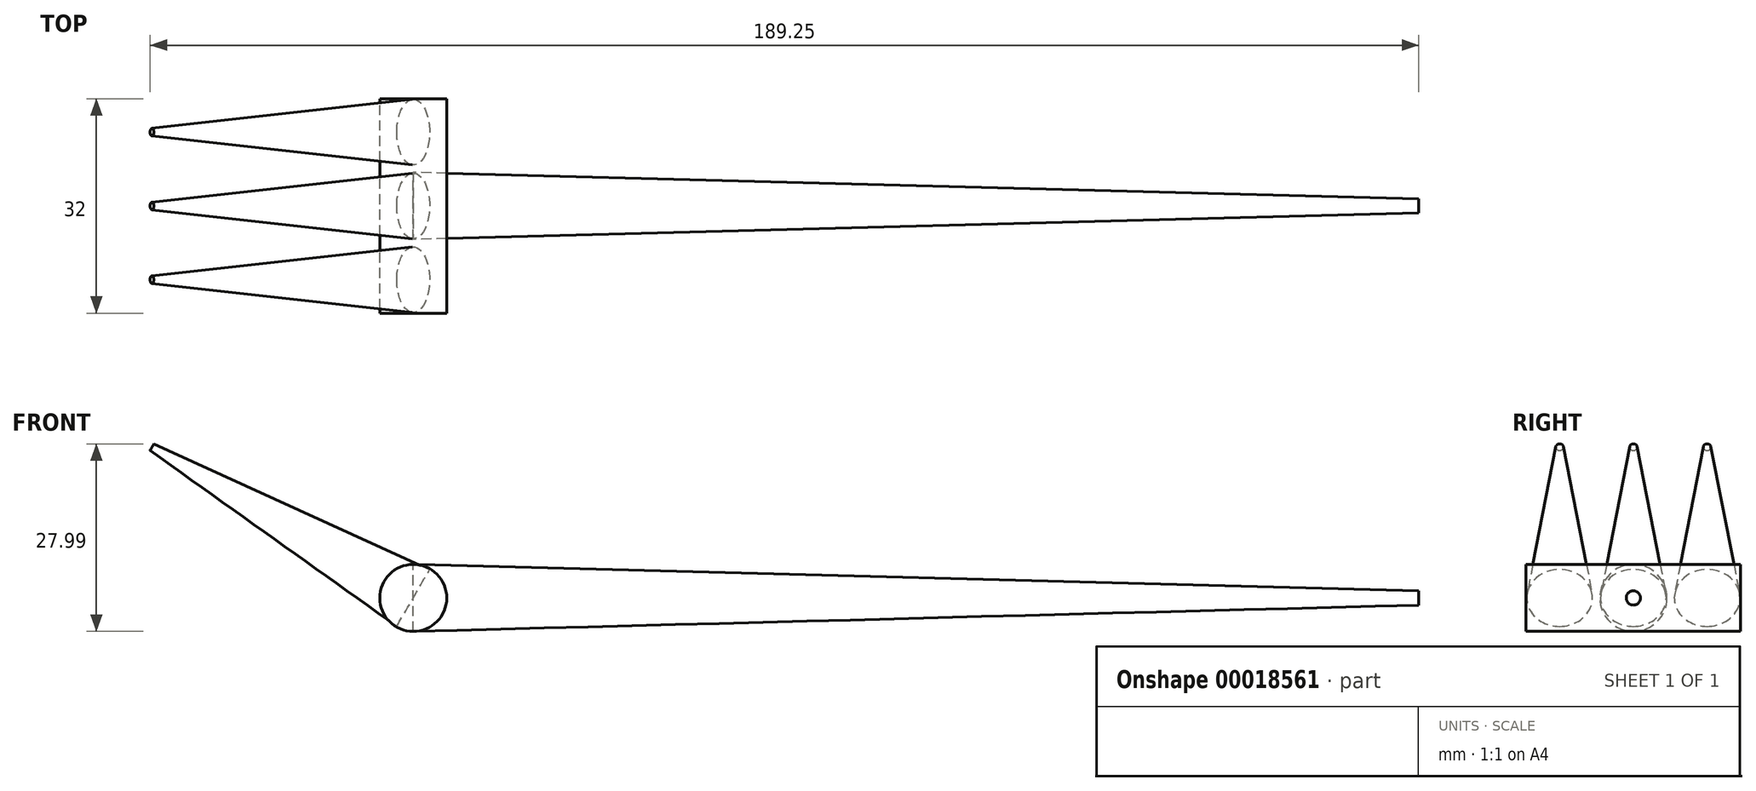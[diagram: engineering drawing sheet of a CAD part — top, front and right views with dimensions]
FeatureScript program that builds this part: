
annotation { "Feature Type Name" : "Feature", "Feature Type Description" : "" }
export const myFeature = defineFeature(function(context is Context, id is Id, definition is map)
    precondition{}
    {
        {
            var Q0;
            Q0=qCreatedBy(makeId("Right.planeOp"),FACE);
            var sketch = newSketch(context, id + "F0", { "sketchPlane" : qUnion([Q0])});
            skCircle(sketch, "E0", {"center": v(0, 0) * mm, "radius": 5 * mm});
            skSolve(sketch);
        }
        {
            var Q0;
            Q0=makeQuery(id+"F0.imprint","IMPRINT",FACE,{"disambiguationData":[TD([[makeQuery(id+"F0.imprint","IMPRINT",EDGE,{"derivedFrom":sQuery(id+"F0.wireOp",EDGE,"E0")}),1.0]])]});
            var Q1;
            Q1=sQuery(id+"F0.wireOp",EDGE,"E0");
            extrude(context, id + "F1", {"entities" : qUnion([Q0]), "surfaceEntities" : qUnion([Q1]), "depth" : 150 * mm, "hasDraft" : true, "draftAngle" : 1.5 * degree, "draftPullDirection" : true});
        }
        {
            var Q0;
            Q0=qCreatedBy(makeId("Front.planeOp"),FACE);
            var sketch = newSketch(context, id + "F2", { "sketchPlane" : qUnion([Q0])});
            skCircle(sketch, "E1", {"center": v(0, 0) * mm, "radius": 5 * mm});
            skSolve(sketch);
        }
        {
            var Q0;
            Q0 = qSketchRegion(id + "F2", true);
            extrude(context, id + "F3", {"entities" : qUnion([Q0]), "depth" : 16 * mm, "hasSecondDirection" : true, "secondDirectionOppositeDirection" : true, "secondDirectionDepth" : 16 * mm});
        }
        {
            var Q0;
            Q0=qCreatedBy(makeId("Right.planeOp"),FACE);
            var sketch = newSketch(context, id + "F4", { "sketchPlane" : qUnion([Q0])});
            skCircle(sketch, "E2", {"center": v(0, 0) * mm, "radius": 4.9 * mm});
            skSolve(sketch);
        }
        {
            var Q0;
            Q0 = qSketchRegion(id + "F4", true);
            extrude(context, id + "F5", {"entities" : qUnion([Q0]), "oppositeDirection" : true, "depth" : 45 * mm, "hasDraft" : true, "draftAngle" : 5.5 * degree, "draftPullDirection" : true});
        }
        {
            var Q0;
            Q0=makeQuery(id+"F5.opExtrude","SWEPT_BODY",BODY,{"disambiguationData":[OSD([sQuery(id+"F4.wireOp",EDGE,"E2")])]});
            var Q1;
            Q1=qCreatedBy(makeId("Front.planeOp"),FACE);
            transform(context, id + "F6", {"entities" : qUnion([Q0]), "transformType" : TransformType.TRANSLATION_DISTANCE, "transformDirection" : qUnion([Q1]), "distance" : 12.5 * mm, "makeCopy" : true});
        }
        {
            var Q0;
            Q0=makeQuery(id+"F6.opPattern","COPY",BODY,{"derivedFrom":makeQuery(id+"F5.opExtrude","SWEPT_BODY",BODY,{"disambiguationData":[OSD([sQuery(id+"F4.wireOp",EDGE,"E2")])]}),"instanceName":"1"});
            var Q1;
            Q1=qCreatedBy(makeId("Front.planeOp"),FACE);
            transform(context, id + "F7", {"entities" : qUnion([Q0]), "transformType" : TransformType.TRANSLATION_DISTANCE, "transformDirection" : qUnion([Q1]), "distance" : 2 * mm, "oppositeDirection" : true, "makeCopy" : false});
        }
        {
            var Q0;
            Q0=makeQuery(id+"F5.opExtrude","SWEPT_BODY",BODY,{"disambiguationData":[OSD([sQuery(id+"F4.wireOp",EDGE,"E2")])]});
            var Q1;
            Q1=qCreatedBy(makeId("Front.planeOp"),FACE);
            transform(context, id + "F8", {"entities" : qUnion([Q0]), "transformType" : TransformType.TRANSLATION_DISTANCE, "transformDirection" : qUnion([Q1]), "distance" : 10 * mm, "oppositeDirection" : true, "makeCopy" : true});
        }
        {
            var Q0;
            Q0=makeQuery(id+"F8.opPattern","COPY",BODY,{"derivedFrom":makeQuery(id+"F5.opExtrude","SWEPT_BODY",BODY,{"disambiguationData":[OSD([sQuery(id+"F4.wireOp",EDGE,"E2")])]}),"instanceName":"1"});
            var Q1;
            Q1=qCreatedBy(makeId("Front.planeOp"),FACE);
            transform(context, id + "F9", {"entities" : qUnion([Q0]), "transformType" : TransformType.TRANSLATION_DISTANCE, "transformDirection" : qUnion([Q1]), "distance" : 1 * mm, "oppositeDirection" : true, "makeCopy" : false});
        }
        {
            var Q0;
            Q0=makeQuery(id+"F6.opPattern","COPY",BODY,{"derivedFrom":makeQuery(id+"F5.opExtrude","SWEPT_BODY",BODY,{"disambiguationData":[OSD([sQuery(id+"F4.wireOp",EDGE,"E2")])]}),"instanceName":"1"});
            var Q1;
            Q1=qCreatedBy(makeId("Front.planeOp"),FACE);
            transform(context, id + "F10", {"entities" : qUnion([Q0]), "transformType" : TransformType.TRANSLATION_DISTANCE, "transformDirection" : qUnion([Q1]), "distance" : 0.5 * mm, "makeCopy" : false});
        }
        {
            var Q0;
            Q0=makeQuery(id+"F8.opPattern","COPY",BODY,{"derivedFrom":makeQuery(id+"F5.opExtrude","SWEPT_BODY",BODY,{"disambiguationData":[OSD([sQuery(id+"F4.wireOp",EDGE,"E2")])]}),"instanceName":"1"});
            var Q1;
            Q1=makeQuery(id+"F5.opExtrude","SWEPT_BODY",BODY,{"disambiguationData":[OSD([sQuery(id+"F4.wireOp",EDGE,"E2")])]});
            var Q2;
            Q2=makeQuery(id+"F6.opPattern","COPY",BODY,{"derivedFrom":makeQuery(id+"F5.opExtrude","SWEPT_BODY",BODY,{"disambiguationData":[OSD([sQuery(id+"F4.wireOp",EDGE,"E2")])]}),"instanceName":"1"});
            var Q3;
            Q3=makeQuery(id+"F3.opExtrude","SWEPT_FACE",FACE,{"disambiguationData":[OSD([sQuery(id+"F2.wireOp",EDGE,"E1")])]});
            transform(context, id + "F11", {"entities" : qUnion([Q0, Q1, Q2]), "transformType" : TransformType.ROTATION, "transformAxis" : qUnion([Q3]), "angle" : 30 * degree, "makeCopy" : false});
        }
    });
